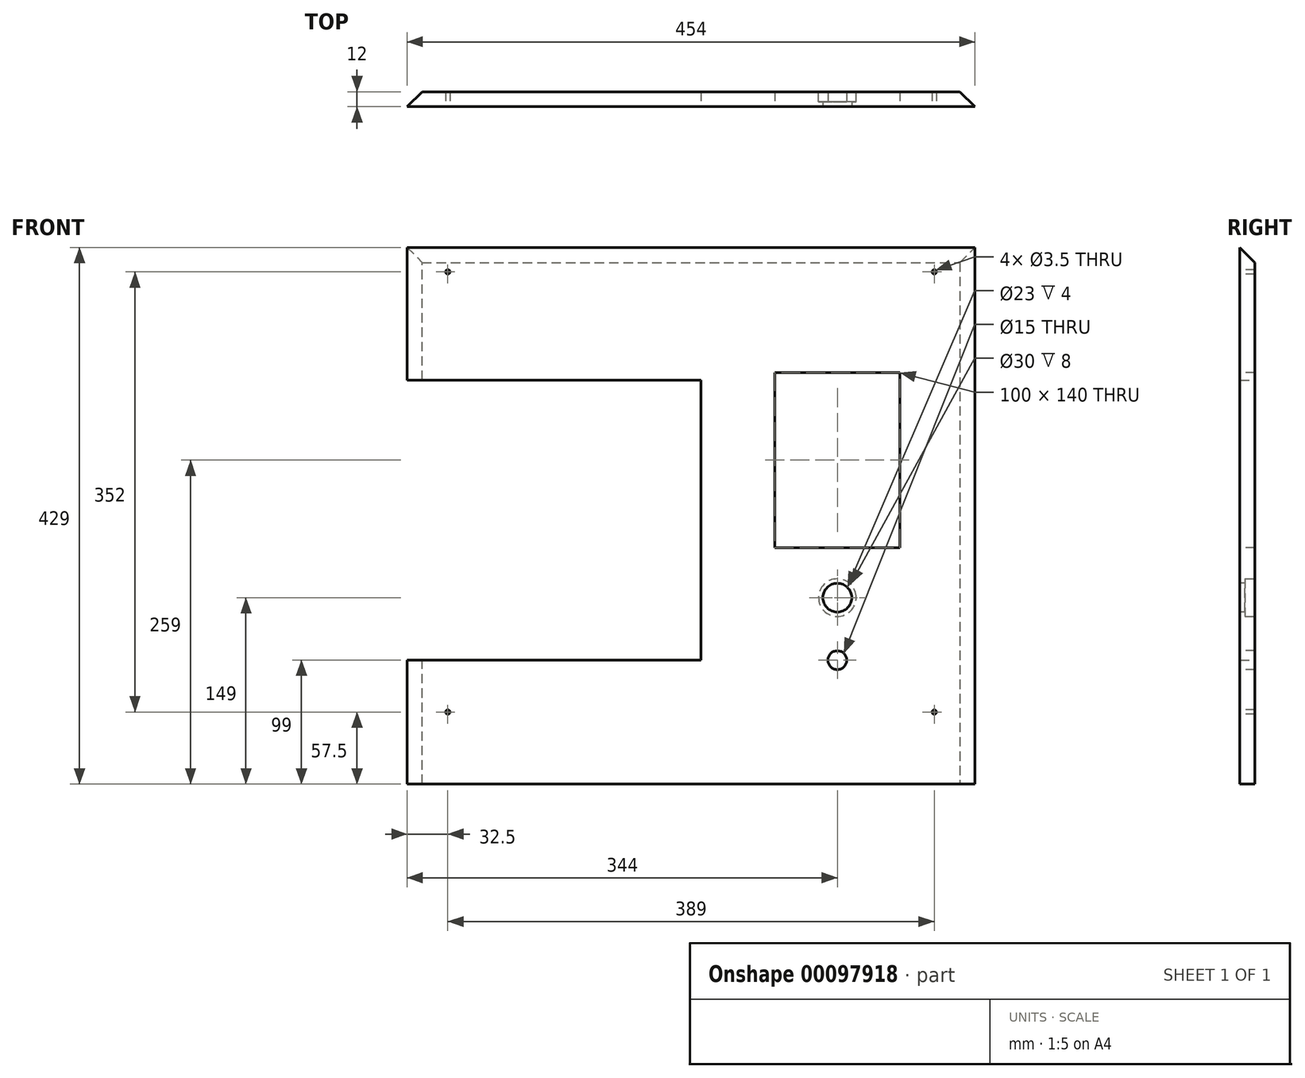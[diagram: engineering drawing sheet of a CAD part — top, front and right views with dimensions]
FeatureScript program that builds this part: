
annotation { "Feature Type Name" : "Feature", "Feature Type Description" : "" }
export const myFeature = defineFeature(function(context is Context, id is Id, definition is map)
    precondition{}
    {
        {
            var Q0;
            Q0=qCreatedBy(makeId("Front.planeOp"),FACE);
            var sketch = newSketch(context, id + "F0", { "sketchPlane" : qUnion([Q0])});
            skLineSegment(sketch, "E0.bottom", {"start": v(-227, 214.5) * mm, "end": v(227, 214.5) * mm});
            skLineSegment(sketch, "E0.top", {"start": v(-227, -214.5) * mm, "end": v(227, -214.5) * mm});
            skLineSegment(sketch, "E0.left", {"start": v(-227, 214.5) * mm, "end": v(-227, -214.5) * mm});
            skLineSegment(sketch, "E0.right", {"start": v(227, 214.5) * mm, "end": v(227, -214.5) * mm});
            skSolve(sketch);
        }
        {
            var Q0;
            Q0=makeQuery(id+"F0.imprint","IMPRINT",FACE,{"disambiguationData":[TD([[makeQuery(id+"F0.imprint","IMPRINT",EDGE,{"derivedFrom":sQuery(id+"F0.wireOp",EDGE,"E0.bottom")}),-1.0]])]});
            extrude(context, id + "F1", {"entities" : qUnion([Q0]), "depth" : 12 * mm});
        }
        {
            var Q0;
            Q0=makeQuery(id+"F1.opExtrude","CAP_EDGE",EDGE,{"disambiguationData":[OSD([sQuery(id+"F0.wireOp",EDGE,"E0.right")])],"isStart":true});
            var Q1;
            Q1=makeQuery(id+"F1.opExtrude","CAP_EDGE",EDGE,{"disambiguationData":[OSD([sQuery(id+"F0.wireOp",EDGE,"E0.left")])],"isStart":true});
            var Q2;
            Q2=makeQuery(id+"F1.opExtrude","CAP_EDGE",EDGE,{"disambiguationData":[OSD([sQuery(id+"F0.wireOp",EDGE,"E0.bottom")])],"isStart":true});
            chamfer(context, id + "F2", {"entities" : qUnion([Q0, Q1, Q2]), "width" : 12 * mm, "tangentPropagation" : true});
        }
        {
            var Q0;
            Q0=makeQuery(id+"F1.opExtrude","CAP_FACE",FACE,{"disambiguationData":[OSD([sQuery(id+"F0.wireOp",EDGE,"E0.bottom"),sQuery(id+"F0.wireOp",EDGE,"E0.top"),sQuery(id+"F0.wireOp",EDGE,"E0.left"),sQuery(id+"F0.wireOp",EDGE,"E0.right")])],"isStart":false});
            var sketch = newSketch(context, id + "F3", { "sketchPlane" : qUnion([Q0])});
            skLineSegment(sketch, "E1.bottom", {"start": v(67, 114.5) * mm, "end": v(167, 114.5) * mm});
            skLineSegment(sketch, "E1.top", {"start": v(67, -25.5) * mm, "end": v(167, -25.5) * mm});
            skLineSegment(sketch, "E1.left", {"start": v(67, 114.5) * mm, "end": v(67, -25.5) * mm});
            skLineSegment(sketch, "E1.right", {"start": v(167, 114.5) * mm, "end": v(167, -25.5) * mm});
            skLineSegment(sketch, "E2.bottom", {"start": v(-227, 108.5) * mm, "end": v(8, 108.5) * mm});
            skLineSegment(sketch, "E2.top", {"start": v(-227, -115.5) * mm, "end": v(8, -115.5) * mm});
            skLineSegment(sketch, "E2.left", {"start": v(-227, 108.5) * mm, "end": v(-227, -115.5) * mm});
            skLineSegment(sketch, "E2.right", {"start": v(8, 108.5) * mm, "end": v(8, -115.5) * mm});
            skCircle(sketch, "E3", {"center": v(117, -65.5) * mm, "radius": 11.5 * mm});
            skPoint(sketch, "E3.centerSnap0", {"position": v(117, -25.5) * mm});
            skCircle(sketch, "E4", {"center": v(117, -115.5) * mm, "radius": 7.5 * mm});
            skSolve(sketch);
        }
        {
            var Q0;
            Q0=makeQuery(id+"F3.imprint","IMPRINT",FACE,{"disambiguationData":[TD([[makeQuery(id+"F3.imprint","IMPRINT",EDGE,{"derivedFrom":sQuery(id+"F3.wireOp",EDGE,"E2.bottom")}),-1.0]])]});
            var Q1;
            Q1=makeQuery(id+"F3.imprint","IMPRINT",FACE,{"disambiguationData":[TD([[makeQuery(id+"F3.imprint","IMPRINT",EDGE,{"derivedFrom":sQuery(id+"F3.wireOp",EDGE,"E1.bottom")}),-1.0]])]});
            var Q2;
            Q2=makeQuery(id+"F3.imprint","IMPRINT",FACE,{"disambiguationData":[TD([[makeQuery(id+"F3.imprint","IMPRINT",EDGE,{"derivedFrom":sQuery(id+"F3.wireOp",EDGE,"E3")}),1.0]])]});
            var Q3;
            Q3=makeQuery(id+"F3.imprint","IMPRINT",FACE,{"disambiguationData":[TD([[makeQuery(id+"F3.imprint","IMPRINT",EDGE,{"derivedFrom":sQuery(id+"F3.wireOp",EDGE,"E4")}),1.0]])]});
            extrude(context, id + "F4", {"entities" : qUnion([Q0, Q1, Q2, Q3]), "operationType" : NewBodyOperationType.REMOVE, "oppositeDirection" : true, "depth" : 25 * mm});
        }
        {
            var Q0;
            Q0=makeQuery(id+"F1.opExtrude","CAP_FACE",FACE,{"disambiguationData":[OSD([sQuery(id+"F0.wireOp",EDGE,"E0.bottom"),sQuery(id+"F0.wireOp",EDGE,"E0.top"),sQuery(id+"F0.wireOp",EDGE,"E0.left"),sQuery(id+"F0.wireOp",EDGE,"E0.right")])],"isStart":false});
            var sketch = newSketch(context, id + "F5", { "sketchPlane" : qUnion([Q0])});
            skLineSegment(sketch, "E5.0", {"start": v(-207.5, 195) * mm, "end": v(-207.5, 108.5) * mm, "construction": true});
            skLineSegment(sketch, "E5.1", {"start": v(-207.5, -115.5) * mm, "end": v(-207.5, -195) * mm, "construction": true});
            skLineSegment(sketch, "E5.2", {"start": v(-207.5, -195) * mm, "end": v(207.5, -195) * mm, "construction": true});
            skLineSegment(sketch, "E5.3", {"start": v(207.5, 195) * mm, "end": v(207.5, -195) * mm, "construction": true});
            skLineSegment(sketch, "E5.4", {"start": v(-207.5, 195) * mm, "end": v(207.5, 195) * mm, "construction": true});
            skLineSegment(sketch, "E6.0", {"start": v(-194.5, 182) * mm, "end": v(-194.5, 108.5) * mm, "construction": true});
            skLineSegment(sketch, "E6.1", {"start": v(-194.5, -115.5) * mm, "end": v(-194.5, -182) * mm, "construction": true});
            skLineSegment(sketch, "E6.2", {"start": v(-194.5, -182) * mm, "end": v(194.5, -182) * mm, "construction": true});
            skLineSegment(sketch, "E6.3", {"start": v(194.5, 182) * mm, "end": v(194.5, -182) * mm, "construction": true});
            skLineSegment(sketch, "E6.4", {"start": v(-194.5, 182) * mm, "end": v(194.5, 182) * mm, "construction": true});
            skLineSegment(sketch, "E7", {"start": v(-194.5, -157) * mm, "end": v(194.5, -157) * mm, "construction": true});
            skPoint(sketch, "E8", {"position": v(-194.5, 195) * mm});
            skPoint(sketch, "E9", {"position": v(194.5, 195) * mm});
            skSolve(sketch);
        }
        {
            var Q0;
            Q0=sQuery(id+"F5.wireOp",VERTEX,"E8");
            var Q1;
            Q1=sQuery(id+"F5.wireOp",VERTEX,"E9");
            var Q2;
            Q2=sQuery(id+"F5.wireOp",VERTEX,"E7.end");
            var Q3;
            Q3=sQuery(id+"F5.wireOp",VERTEX,"E7.start");
            var Q4;
            Q4=makeQuery(id+"F1.opExtrude","SWEPT_BODY",BODY,{"disambiguationData":[OSD([sQuery(id+"F0.wireOp",EDGE,"E0.bottom"),sQuery(id+"F0.wireOp",EDGE,"E0.top"),sQuery(id+"F0.wireOp",EDGE,"E0.left"),sQuery(id+"F0.wireOp",EDGE,"E0.right")])]});
            hole(context, id + "F6", {"style" : HoleStyle.SIMPLE, "endStyle" : HoleEndStyle.THROUGH, "holeDiameter" : 3.5 * mm, "locations" : qUnion([Q0, Q1, Q2, Q3]), "scope" : qUnion([Q4]), "isTappedThrough" : true});
        }
        {
            var Q0;
            Q0=makeQuery(id+"F1.opExtrude","CAP_FACE",FACE,{"disambiguationData":[OSD([sQuery(id+"F0.wireOp",EDGE,"E0.bottom"),sQuery(id+"F0.wireOp",EDGE,"E0.top"),sQuery(id+"F0.wireOp",EDGE,"E0.left"),sQuery(id+"F0.wireOp",EDGE,"E0.right")])],"isStart":true});
            var sketch = newSketch(context, id + "F7", { "sketchPlane" : qUnion([Q0])});
            skCircle(sketch, "E10.0", {"center": v(-117, -65.5) * mm, "radius": 11.5 * mm});
            skCircle(sketch, "E11", {"center": v(-117, -65.5) * mm, "radius": 15 * mm});
            skSolve(sketch);
        }
        {
            var Q0;
            Q0 = qSketchRegion(id + "F7", true);
            extrude(context, id + "F8", {"entities" : qUnion([Q0]), "operationType" : NewBodyOperationType.REMOVE, "oppositeDirection" : true, "depth" : 8 * mm});
        }
    });
